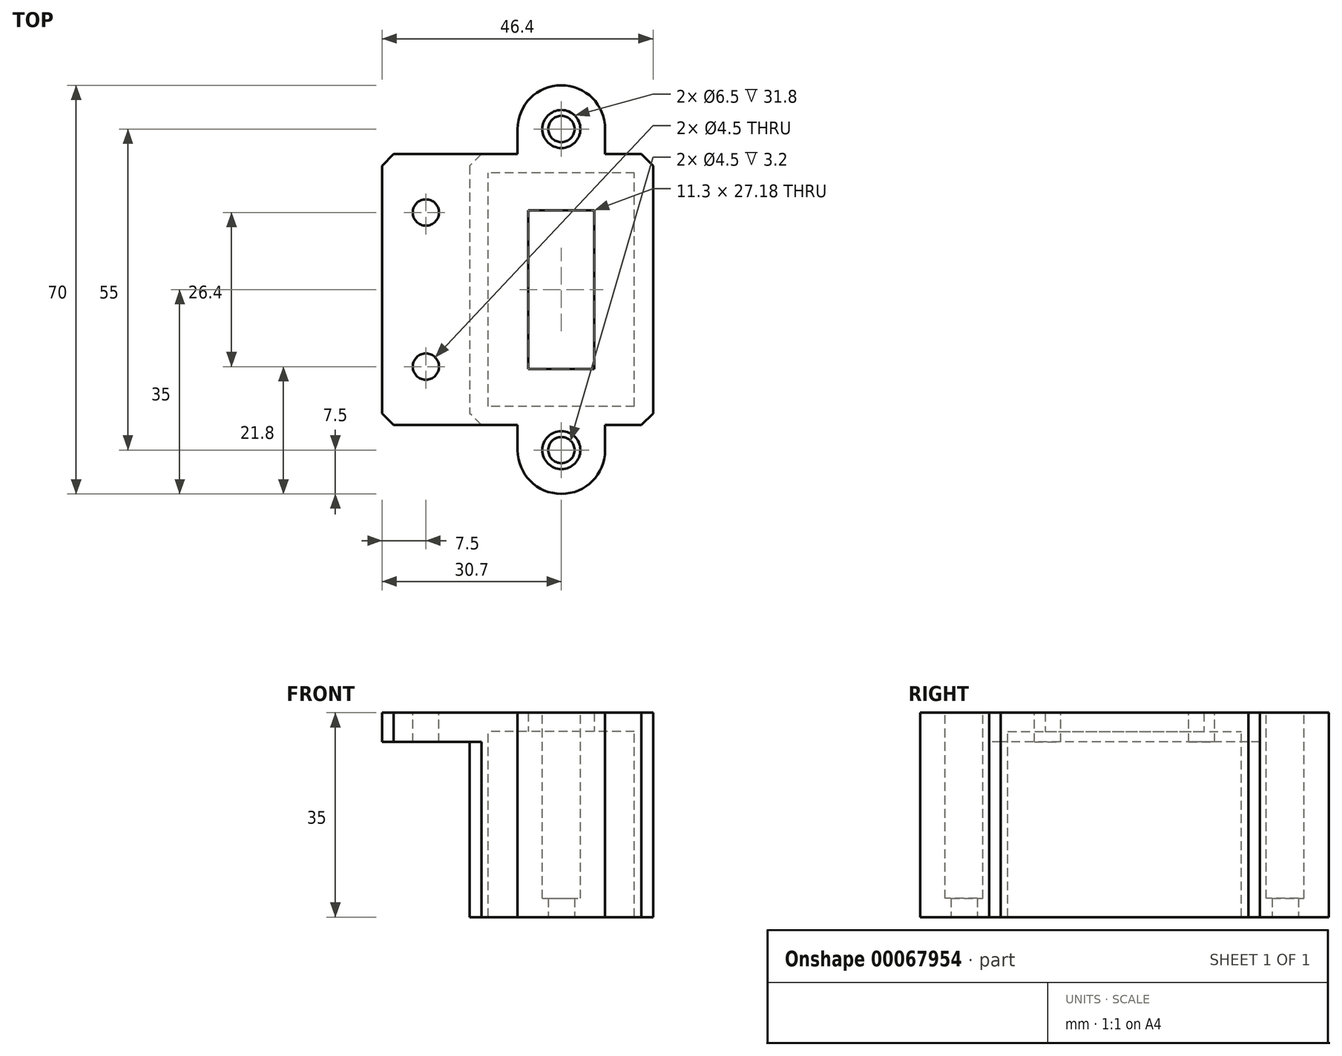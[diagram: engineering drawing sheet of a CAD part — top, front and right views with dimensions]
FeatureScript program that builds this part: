
annotation { "Feature Type Name" : "Feature", "Feature Type Description" : "" }
export const myFeature = defineFeature(function(context is Context, id is Id, definition is map)
    precondition{}
    {
        {
            var Q0;
            Q0=qCreatedBy(makeId("Top.planeOp"),FACE);
            var sketch = newSketch(context, id + "F0", { "sketchPlane" : qUnion([Q0])});
            skLineSegment(sketch, "E0.rect.bottom", {"start": v(12.5, -20) * mm, "end": v(-12.5, -20) * mm});
            skLineSegment(sketch, "E0.rect.top", {"start": v(12.5, 20) * mm, "end": v(-12.5, 20) * mm});
            skLineSegment(sketch, "E0.rect.left", {"start": v(12.5, -20) * mm, "end": v(12.5, 20) * mm});
            skLineSegment(sketch, "E0.rect.right", {"start": v(-12.5, -20) * mm, "end": v(-12.5, 20) * mm});
            skPoint(sketch, "E0.rect.middle", {"position": v(0, 0) * mm});
            skLineSegment(sketch, "E1.bottom", {"start": v(5.65, -13.59) * mm, "end": v(-5.65, -13.59) * mm});
            skLineSegment(sketch, "E1.top", {"start": v(5.65, 13.59) * mm, "end": v(-5.65, 13.59) * mm});
            skLineSegment(sketch, "E1.left", {"start": v(5.65, -13.59) * mm, "end": v(5.65, 13.59) * mm});
            skLineSegment(sketch, "E1.right", {"start": v(-5.65, -13.59) * mm, "end": v(-5.65, 13.59) * mm});
            skSolve(sketch);
        }
        {
            var Q0;
            Q0=qSketchRegion(id+"F0",true);
            extrude(context, id + "F1", {"entities" : qUnion([Q0]), "depth" : 3.2 * mm});
        }
        {
            var Q0;
            Q0=makeQuery(id+"F1.opExtrude","CAP_FACE",FACE,{"disambiguationData":[OSD([sQuery(id+"F0.wireOp",EDGE,"E0.rect.bottom"),sQuery(id+"F0.wireOp",EDGE,"E0.rect.top"),sQuery(id+"F0.wireOp",EDGE,"E0.rect.left"),sQuery(id+"F0.wireOp",EDGE,"E0.rect.right"),sQuery(id+"F0.wireOp",EDGE,"209dc2e6-67a9-4a65-bd37-3dd2c5807d82")])],"isStart":false});
            var sketch = newSketch(context, id + "F2", { "sketchPlane" : qUnion([Q0])});
            skLineSegment(sketch, "E2.rect.bottom", {"start": v(12.5, 20) * mm, "end": v(-12.5, 20) * mm});
            skLineSegment(sketch, "E2.rect.top", {"start": v(12.5, -20) * mm, "end": v(-12.5, -20) * mm});
            skLineSegment(sketch, "E2.rect.left", {"start": v(12.5, 20) * mm, "end": v(12.5, -20) * mm});
            skLineSegment(sketch, "E2.rect.right", {"start": v(-12.5, 20) * mm, "end": v(-12.5, -20) * mm});
            skPoint(sketch, "E2.rect.middle", {"position": v(0, 0) * mm});
            skLineSegment(sketch, "E3.rect.bottom", {"start": v(15.7, 23.2) * mm, "end": v(7.5, 23.2) * mm});
            skLineSegment(sketch, "E3.rect.left", {"start": v(15.7, 23.2) * mm, "end": v(15.7, -23.2) * mm});
            skLineSegment(sketch, "E3.rect.right", {"start": v(-15.7, 23.2) * mm, "end": v(-15.7, -23.2) * mm});
            skLineSegment(sketch, "E4", {"start": v(-7.5, 23.2) * mm, "end": v(-7.5, 27.5) * mm});
            skLineSegment(sketch, "E5", {"start": v(0, 27.5) * mm, "end": v(0, 23.2) * mm});
            skLineSegment(sketch, "E6", {"start": v(0, 0) * mm, "end": v(-6.25, 0) * mm, "construction": true});
            skLineSegment(sketch, "E7.MirrorCS", {"start": v(7.5, 23.2) * mm, "end": v(7.5, 27.5) * mm});
            skArc(sketch, "E8", {"start": v(-7.5, 27.5) * mm, "mid": v(0, 35) * mm, "end": v(7.5, 27.5) * mm});
            skLineSegment(sketch, "E9.MirrorCS", {"start": v(-7.5, -23.2) * mm, "end": v(-7.5, -27.5) * mm});
            skLineSegment(sketch, "E10.MirrorCS", {"start": v(15.7, -23.2) * mm, "end": v(7.5, -23.2) * mm});
            skLineSegment(sketch, "E11.MirrorCS", {"start": v(0, -27.5) * mm, "end": v(0, -23.2) * mm, "construction": true});
            skArc(sketch, "E12.MirrorCS", {"start": v(-7.5, -27.5) * mm, "mid": v(0, -35) * mm, "end": v(7.5, -27.5) * mm});
            skLineSegment(sketch, "E13.MirrorCS", {"start": v(7.5, -23.2) * mm, "end": v(7.5, -27.5) * mm});
            skLineSegment(sketch, "E14.trimOffspring", {"start": v(-7.5, -23.2) * mm, "end": v(-15.7, -23.2) * mm});
            skLineSegment(sketch, "E15.trimOffspring", {"start": v(-7.5, 23.2) * mm, "end": v(-15.7, 23.2) * mm});
            skCircle(sketch, "E16.cCircle", {"center": v(0, 27.5) * mm, "radius": 2.98 * mm, "construction": true});
            skLineSegment(sketch, "E16.0", {"start": v(-1.72, 30.48) * mm, "end": v(1.72, 30.48) * mm, "construction": true});
            skLineSegment(sketch, "E16.1", {"start": v(1.72, 30.48) * mm, "end": v(3.44, 27.5) * mm, "construction": true});
            skLineSegment(sketch, "E16.2", {"start": v(3.44, 27.5) * mm, "end": v(1.72, 24.52) * mm, "construction": true});
            skLineSegment(sketch, "E16.3", {"start": v(1.72, 24.52) * mm, "end": v(-1.72, 24.52) * mm, "construction": true});
            skLineSegment(sketch, "E16.4", {"start": v(-1.72, 24.52) * mm, "end": v(-3.44, 27.5) * mm, "construction": true});
            skLineSegment(sketch, "E16.5", {"start": v(-3.44, 27.5) * mm, "end": v(-1.72, 30.48) * mm, "construction": true});
            skPoint(sketch, "E16.0.midPoint", {"position": v(0, 30.48) * mm});
            skCircle(sketch, "E17.cCircle", {"center": v(0, -27.5) * mm, "radius": 2.98 * mm, "construction": true});
            skLineSegment(sketch, "E17.0", {"start": v(-1.72, -24.52) * mm, "end": v(1.72, -24.52) * mm, "construction": true});
            skLineSegment(sketch, "E17.1", {"start": v(1.72, -24.52) * mm, "end": v(3.44, -27.5) * mm, "construction": true});
            skLineSegment(sketch, "E17.2", {"start": v(3.44, -27.5) * mm, "end": v(1.72, -30.47) * mm, "construction": true});
            skLineSegment(sketch, "E17.3", {"start": v(1.72, -30.48) * mm, "end": v(-1.72, -30.48) * mm, "construction": true});
            skLineSegment(sketch, "E17.4", {"start": v(-1.72, -30.48) * mm, "end": v(-3.44, -27.5) * mm, "construction": true});
            skLineSegment(sketch, "E17.5", {"start": v(-3.44, -27.5) * mm, "end": v(-1.72, -24.52) * mm, "construction": true});
            skPoint(sketch, "E17.0.midPoint", {"position": v(0, -24.52) * mm});
            skCircle(sketch, "E18", {"center": v(0, -27.5) * mm, "radius": 3.25 * mm});
            skCircle(sketch, "E19", {"center": v(0, 27.5) * mm, "radius": 3.25 * mm});
            skSolve(sketch);
        }
        {
            var Q0;
            Q0=qSketchRegion(id+"F2",true);
            extrude(context, id + "F3", {"entities" : qUnion([Q0]), "operationType" : NewBodyOperationType.ADD, "oppositeDirection" : true, "depth" : 35 * mm});
        }
        {
            var Q0;
            Q0=makeQuery(id+"F3.boolean.opBoolean","MERGE",FACE,{"derivedFrom":[makeQuery(id+"F1.opExtrude","CAP_FACE",FACE,{"disambiguationData":[OSD([sQuery(id+"F0.wireOp",EDGE,"E0.rect.bottom"),sQuery(id+"F0.wireOp",EDGE,"E0.rect.top"),sQuery(id+"F0.wireOp",EDGE,"E0.rect.left"),sQuery(id+"F0.wireOp",EDGE,"E0.rect.right"),sQuery(id+"F0.wireOp",EDGE,"209dc2e6-67a9-4a65-bd37-3dd2c5807d82")])],"isStart":false}),makeQuery(id+"F3.opExtrude","CAP_FACE",FACE,{"disambiguationData":[OSD([sQuery(id+"F2.wireOp",EDGE,"E2.rect.bottom"),sQuery(id+"F2.wireOp",EDGE,"E2.rect.top"),sQuery(id+"F2.wireOp",EDGE,"E2.rect.left"),sQuery(id+"F2.wireOp",EDGE,"E2.rect.right"),sQuery(id+"F2.wireOp",EDGE,"E3.rect.bottom"),sQuery(id+"F2.wireOp",EDGE,"E3.rect.top"),sQuery(id+"F2.wireOp",EDGE,"E3.rect.left"),sQuery(id+"F2.wireOp",EDGE,"E3.rect.right")])],"isStart":true})]});
            var sketch = newSketch(context, id + "F4", { "sketchPlane" : qUnion([Q0])});
            skLineSegment(sketch, "E20", {"start": v(-15.7, 23.2) * mm, "end": v(-30.7, 23.2) * mm});
            skLineSegment(sketch, "E21", {"start": v(-30.7, 23.2) * mm, "end": v(-30.7, -23.2) * mm});
            skLineSegment(sketch, "E22", {"start": v(-30.7, -23.2) * mm, "end": v(-15.7, -23.2) * mm});
            skLineSegment(sketch, "E23", {"start": v(-15.7, -23.2) * mm, "end": v(-15.7, 23.2) * mm});
            skCircle(sketch, "E24", {"center": v(-23.2, 13.2) * mm, "radius": 2.25 * mm});
            skCircle(sketch, "E25", {"center": v(-23.2, -13.2) * mm, "radius": 2.25 * mm});
            skPoint(sketch, "E25.centerSnap0", {"position": v(-23.2, -23.2) * mm});
            skSolve(sketch);
        }
        {
            var Q0;
            Q0=qSketchRegion(id+"F4",true);
            extrude(context, id + "F5", {"entities" : qUnion([Q0]), "operationType" : NewBodyOperationType.ADD, "oppositeDirection" : true, "depth" : 5 * mm});
        }
        {
            var Q0;
            Q0=makeQuery(id+"F3.opExtrude","SWEPT_EDGE",EDGE,{"disambiguationData":[OSD([sQuery(id+"F2.wireOp",EDGE,"E3.rect.bottom"),sQuery(id+"F2.wireOp",EDGE,"E3.rect.left")])]});
            var Q1;
            Q1=makeQuery(id+"F3.opExtrude","SWEPT_EDGE",EDGE,{"disambiguationData":[OSD([sQuery(id+"F2.wireOp",EDGE,"E3.rect.right"),sQuery(id+"F2.wireOp",EDGE,"E15.trimOffspring")])]});
            var Q2;
            Q2=makeQuery(id+"F3.opExtrude","SWEPT_EDGE",EDGE,{"disambiguationData":[OSD([sQuery(id+"F2.wireOp",EDGE,"E3.rect.right"),sQuery(id+"F2.wireOp",EDGE,"E14.trimOffspring")])]});
            var Q3;
            Q3=makeQuery(id+"F3.opExtrude","SWEPT_EDGE",EDGE,{"disambiguationData":[OSD([sQuery(id+"F2.wireOp",EDGE,"E3.rect.bottom"),sQuery(id+"F2.wireOp",EDGE,"E3.rect.left")])]});
            var Q4;
            Q4=makeQuery(id+"F3.opExtrude","SWEPT_EDGE",EDGE,{"disambiguationData":[OSD([sQuery(id+"F2.wireOp",EDGE,"E3.rect.bottom"),sQuery(id+"F2.wireOp",EDGE,"E3.rect.left")])]});
            var Q5;
            Q5=makeQuery(id+"F3.opExtrude","SWEPT_EDGE",EDGE,{"disambiguationData":[OSD([sQuery(id+"F2.wireOp",EDGE,"E3.rect.left"),sQuery(id+"F2.wireOp",EDGE,"E10.MirrorCS")])]});
            var Q6;
            Q6=makeQuery(id+"F3.opExtrude","SWEPT_EDGE",EDGE,{"disambiguationData":[OSD([sQuery(id+"F2.wireOp",EDGE,"E3.rect.right"),sQuery(id+"F2.wireOp",EDGE,"E15.trimOffspring")])]});
            var Q7;
            Q7=makeQuery(id+"F3.opExtrude","SWEPT_EDGE",EDGE,{"disambiguationData":[OSD([sQuery(id+"F2.wireOp",EDGE,"E3.rect.right"),sQuery(id+"F2.wireOp",EDGE,"E14.trimOffspring")])]});
            var Q8;
            Q8=makeQuery(id+"F5.opExtrude","SWEPT_EDGE",EDGE,{"disambiguationData":[OSD([sQuery(id+"F4.wireOp",EDGE,"E20"),sQuery(id+"F4.wireOp",EDGE,"E21")])]});
            var Q9;
            Q9=makeQuery(id+"F5.opExtrude","SWEPT_EDGE",EDGE,{"disambiguationData":[OSD([sQuery(id+"F4.wireOp",EDGE,"E21"),sQuery(id+"F4.wireOp",EDGE,"E22")])]});
            chamfer(context, id + "F6", {"entities" : qUnion([Q0, Q1, Q2, Q3, Q4, Q5, Q6, Q7, Q8, Q9]), "width" : 2 * mm, "tangentPropagation" : true});
        }
        {
            var Q0;
            Q0=makeQuery(id+"F3.opExtrude","CAP_FACE",FACE,{"disambiguationData":[OSD([sQuery(id+"F2.wireOp",EDGE,"E2.rect.bottom"),sQuery(id+"F2.wireOp",EDGE,"E2.rect.top"),sQuery(id+"F2.wireOp",EDGE,"E2.rect.left"),sQuery(id+"F2.wireOp",EDGE,"E2.rect.right"),sQuery(id+"F2.wireOp",EDGE,"E3.rect.bottom"),sQuery(id+"F2.wireOp",EDGE,"E3.rect.left"),sQuery(id+"F2.wireOp",EDGE,"E3.rect.right"),sQuery(id+"F2.wireOp",EDGE,"E4"),sQuery(id+"F2.wireOp",EDGE,"E7.MirrorCS"),sQuery(id+"F2.wireOp",EDGE,"E8"),sQuery(id+"F2.wireOp",EDGE,"E9.MirrorCS"),sQuery(id+"F2.wireOp",EDGE,"E10.MirrorCS"),sQuery(id+"F2.wireOp",EDGE,"E12.MirrorCS"),sQuery(id+"F2.wireOp",EDGE,"E13.MirrorCS"),sQuery(id+"F2.wireOp",EDGE,"E14.trimOffspring"),sQuery(id+"F2.wireOp",EDGE,"E15.trimOffspring"),sQuery(id+"F2.wireOp",EDGE,"E16.0"),sQuery(id+"F2.wireOp",EDGE,"E16.1"),sQuery(id+"F2.wireOp",EDGE,"E16.2"),sQuery(id+"F2.wireOp",EDGE,"E16.3"),sQuery(id+"F2.wireOp",EDGE,"E16.4"),sQuery(id+"F2.wireOp",EDGE,"E16.5"),sQuery(id+"F2.wireOp",EDGE,"E17.0"),sQuery(id+"F2.wireOp",EDGE,"E17.1"),sQuery(id+"F2.wireOp",EDGE,"E17.2"),sQuery(id+"F2.wireOp",EDGE,"E17.3"),sQuery(id+"F2.wireOp",EDGE,"E17.4"),sQuery(id+"F2.wireOp",EDGE,"E17.5")])],"isStart":false});
            var sketch = newSketch(context, id + "F7", { "sketchPlane" : qUnion([Q0])});
            skLineSegment(sketch, "E26", {"start": v(0, 0) * mm, "end": v(12.5, 0) * mm, "construction": true});
            skCircle(sketch, "E27", {"center": v(0, 27.5) * mm, "radius": 2.25 * mm});
            skCircle(sketch, "E28.MirrorC", {"center": v(0, -27.5) * mm, "radius": 3.25 * mm, "construction": true});
            skCircle(sketch, "E29.MirrorC", {"center": v(0, -27.5) * mm, "radius": 2.25 * mm});
            skCircle(sketch, "E30", {"center": v(0, -27.5) * mm, "radius": 3.25 * mm});
            skCircle(sketch, "E31", {"center": v(0, 27.5) * mm, "radius": 3.25 * mm});
            skSolve(sketch);
        }
        {
            var Q0;
            Q0=qSketchRegion(id+"F7",true);
            extrude(context, id + "F8", {"entities" : qUnion([Q0]), "operationType" : NewBodyOperationType.ADD, "oppositeDirection" : true, "depth" : 3.2 * mm});
        }
    });
